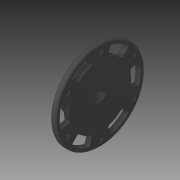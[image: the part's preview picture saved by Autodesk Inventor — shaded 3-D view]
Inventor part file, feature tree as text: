
AUTODESK INVENTOR PART (.ipt)
format: ipt  version: 2019 (Build 230136000, 136)  size: 208,896 bytes
history: native  units: in
note: dims shown in document units (in); Inventor stores cm internally (conversion verified against a paired STEP export)
features: chamfer x1
ambient origin geometry x8: Origin, YZ Plane, XZ Plane, XY Plane, X Axis, Y Axis, Z Axis, Center Point
bodies: Solid1 (feature_tree)
feature tree (1):
  chamfer  "Chamfer1"  [1 undecoded]
note: 1 required parameter value undecoded (feature->parameter linkage not recoverable at this tier; creation-order binding heuristic only, values carry confidence <= 0.55)
